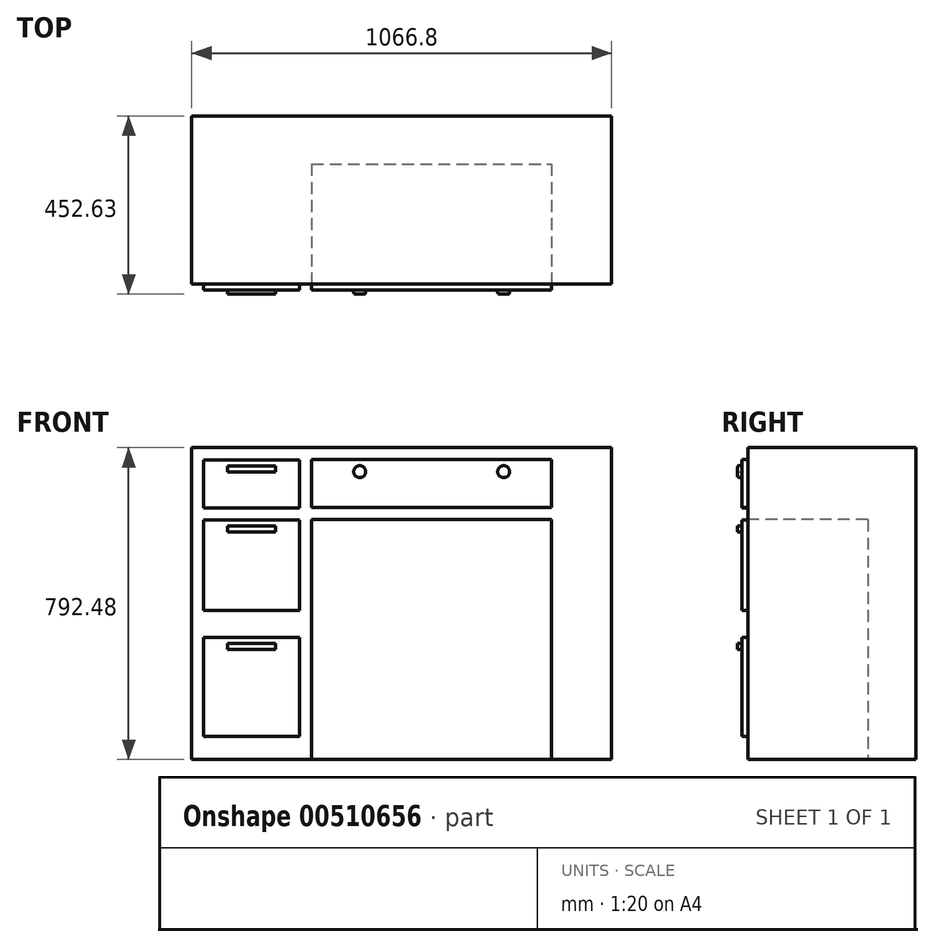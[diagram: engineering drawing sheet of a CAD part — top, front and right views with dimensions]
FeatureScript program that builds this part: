
annotation { "Feature Type Name" : "Feature", "Feature Type Description" : "" }
export const myFeature = defineFeature(function(context is Context, id is Id, definition is map)
    precondition{}
    {
        {
            var Q0;
            Q0=qCreatedBy(makeId("Top.planeOp"),FACE);
            var sketch = newSketch(context, id + "F0", { "sketchPlane" : qUnion([Q0])});
            skLineSegment(sketch, "E0.bottom", {"start": v(-532.21, 166.97) * mm, "end": v(534.59, 166.97) * mm});
            skLineSegment(sketch, "E0.top", {"start": v(-532.21, -259.75) * mm, "end": v(534.59, -259.75) * mm});
            skLineSegment(sketch, "E0.left", {"start": v(-532.21, 166.97) * mm, "end": v(-532.21, -259.75) * mm});
            skLineSegment(sketch, "E0.right", {"start": v(534.59, 166.97) * mm, "end": v(534.59, -259.75) * mm});
            skSolve(sketch);
        }
        {
            var Q0;
            Q0 = qSketchRegion(id + "F0", true);
            extrude(context, id + "F1", {"entities" : qUnion([Q0]), "depth" : 792.48 * mm, "offsetDistance" : 30.48 * mm});
        }
        {
            var Q0;
            Q0=makeQuery(id+"F1.opExtrude","SWEPT_FACE",FACE,{"disambiguationData":[OSD([sQuery(id+"F0.wireOp",EDGE,"E0.top")])]});
            var sketch = newSketch(context, id + "F2", { "sketchPlane" : qUnion([Q0])});
            skLineSegment(sketch, "E1.bottom", {"start": v(-227.41, 609.6) * mm, "end": v(382.19, 609.6) * mm});
            skLineSegment(sketch, "E1.top", {"start": v(-227.41, 0) * mm, "end": v(382.19, 0) * mm});
            skLineSegment(sketch, "E1.left", {"start": v(-227.41, 609.6) * mm, "end": v(-227.41, 0) * mm});
            skLineSegment(sketch, "E1.right", {"start": v(382.19, 609.6) * mm, "end": v(382.19, 0) * mm});
            skSolve(sketch);
        }
        {
            var Q0;
            Q0 = qSketchRegion(id + "F2", true);
            extrude(context, id + "F3", {"entities" : qUnion([Q0]), "operationType" : NewBodyOperationType.REMOVE, "oppositeDirection" : true, "depth" : 304.8 * mm, "offsetDistance" : 30.48 * mm});
        }
        {
            var Q0;
            Q0=makeQuery(id+"F1.opExtrude","SWEPT_FACE",FACE,{"disambiguationData":[OSD([sQuery(id+"F0.wireOp",EDGE,"E0.top")])]});
            var sketch = newSketch(context, id + "F4", { "sketchPlane" : qUnion([Q0])});
            skLineSegment(sketch, "E2.bottom", {"start": v(-227.41, 762) * mm, "end": v(382.19, 762) * mm});
            skLineSegment(sketch, "E2.top", {"start": v(-227.41, 640.08) * mm, "end": v(382.19, 640.08) * mm});
            skLineSegment(sketch, "E2.left", {"start": v(-227.41, 762) * mm, "end": v(-227.41, 640.08) * mm});
            skLineSegment(sketch, "E2.right", {"start": v(382.19, 762) * mm, "end": v(382.19, 640.08) * mm});
            skLineSegment(sketch, "E3.bottom", {"start": v(-501.73, 761.33) * mm, "end": v(-257.9, 761.33) * mm});
            skLineSegment(sketch, "E3.top", {"start": v(-501.73, 639.4) * mm, "end": v(-257.9, 639.4) * mm});
            skLineSegment(sketch, "E3.left", {"start": v(-501.73, 761.33) * mm, "end": v(-501.73, 639.4) * mm});
            skLineSegment(sketch, "E3.right", {"start": v(-257.9, 761.33) * mm, "end": v(-257.9, 639.4) * mm});
            skLineSegment(sketch, "E4.bottom", {"start": v(-501.73, 608.93) * mm, "end": v(-257.9, 608.93) * mm});
            skLineSegment(sketch, "E4.top", {"start": v(-501.73, 379.06) * mm, "end": v(-257.9, 379.06) * mm});
            skLineSegment(sketch, "E4.left", {"start": v(-501.73, 608.93) * mm, "end": v(-501.73, 379.06) * mm});
            skLineSegment(sketch, "E4.right", {"start": v(-257.9, 608.93) * mm, "end": v(-257.9, 379.06) * mm});
            skLineSegment(sketch, "E5.bottom", {"start": v(-501.73, 310.78) * mm, "end": v(-257.9, 310.78) * mm});
            skLineSegment(sketch, "E5.top", {"start": v(-501.73, 58.15) * mm, "end": v(-257.9, 58.15) * mm});
            skLineSegment(sketch, "E5.left", {"start": v(-501.73, 310.78) * mm, "end": v(-501.73, 58.15) * mm});
            skLineSegment(sketch, "E5.right", {"start": v(-257.9, 310.78) * mm, "end": v(-257.9, 58.15) * mm});
            skSolve(sketch);
        }
        {
            var Q0;
            Q0 = qSketchRegion(id + "F4", true);
            extrude(context, id + "F5", {"entities" : qUnion([Q0]), "operationType" : NewBodyOperationType.ADD, "depth" : 15.24 * mm, "offsetDistance" : 30.48 * mm});
        }
        {
            var Q0;
            Q0=makeQuery(id+"F1.opExtrude","SWEPT_FACE",FACE,{"disambiguationData":[OSD([sQuery(id+"F0.wireOp",EDGE,"E0.top")])]});
            var sketch = newSketch(context, id + "F6", { "sketchPlane" : qUnion([Q0])});
            skLineSegment(sketch, "E6.bottom", {"start": v(-440.77, 746.09) * mm, "end": v(-318.85, 746.09) * mm});
            skLineSegment(sketch, "E6.top", {"start": v(-440.77, 730.85) * mm, "end": v(-318.85, 730.85) * mm});
            skLineSegment(sketch, "E6.left", {"start": v(-440.77, 746.09) * mm, "end": v(-440.77, 730.85) * mm});
            skLineSegment(sketch, "E6.right", {"start": v(-318.85, 746.09) * mm, "end": v(-318.85, 730.85) * mm});
            skLineSegment(sketch, "E7.bottom", {"start": v(-440.77, 593.69) * mm, "end": v(-318.85, 593.69) * mm});
            skLineSegment(sketch, "E7.top", {"start": v(-440.77, 578.45) * mm, "end": v(-318.85, 578.45) * mm});
            skLineSegment(sketch, "E7.left", {"start": v(-440.77, 593.69) * mm, "end": v(-440.77, 578.45) * mm});
            skLineSegment(sketch, "E7.right", {"start": v(-318.85, 593.69) * mm, "end": v(-318.85, 578.45) * mm});
            skLineSegment(sketch, "E8.bottom", {"start": v(-440.77, 295.54) * mm, "end": v(-318.85, 295.54) * mm});
            skLineSegment(sketch, "E8.top", {"start": v(-440.77, 280.3) * mm, "end": v(-318.85, 280.3) * mm});
            skLineSegment(sketch, "E8.left", {"start": v(-440.77, 295.54) * mm, "end": v(-440.77, 280.3) * mm});
            skLineSegment(sketch, "E8.right", {"start": v(-318.85, 295.54) * mm, "end": v(-318.85, 280.3) * mm});
            skCircle(sketch, "E9", {"center": v(-105.5, 731.52) * mm, "radius": 15.24 * mm});
            skCircle(sketch, "E10", {"center": v(260.27, 731.52) * mm, "radius": 15.24 * mm});
            skSolve(sketch);
        }
        {
            var Q0;
            Q0 = qSketchRegion(id + "F6", true);
            extrude(context, id + "F7", {"entities" : qUnion([Q0]), "operationType" : NewBodyOperationType.ADD, "depth" : 25.9 * mm, "offsetDistance" : 30.48 * mm});
        }
        {
            var Q0;
            Q0=makeQuery(id+"F7.opExtrude","CAP_EDGE",EDGE,{"disambiguationData":[OSD([sQuery(id+"F6.wireOp",EDGE,"E9")])],"isStart":false});
            var Q1;
            Q1=makeQuery(id+"F7.opExtrude","CAP_EDGE",EDGE,{"disambiguationData":[OSD([sQuery(id+"F6.wireOp",EDGE,"E10")])],"isStart":false});
            fillet(context, id + "F8", {"entities" : qUnion([Q0, Q1]), "radius" : 4.57 * mm, "tangentPropagation" : true, "allowEdgeOverflow" : false});
        }
    });
